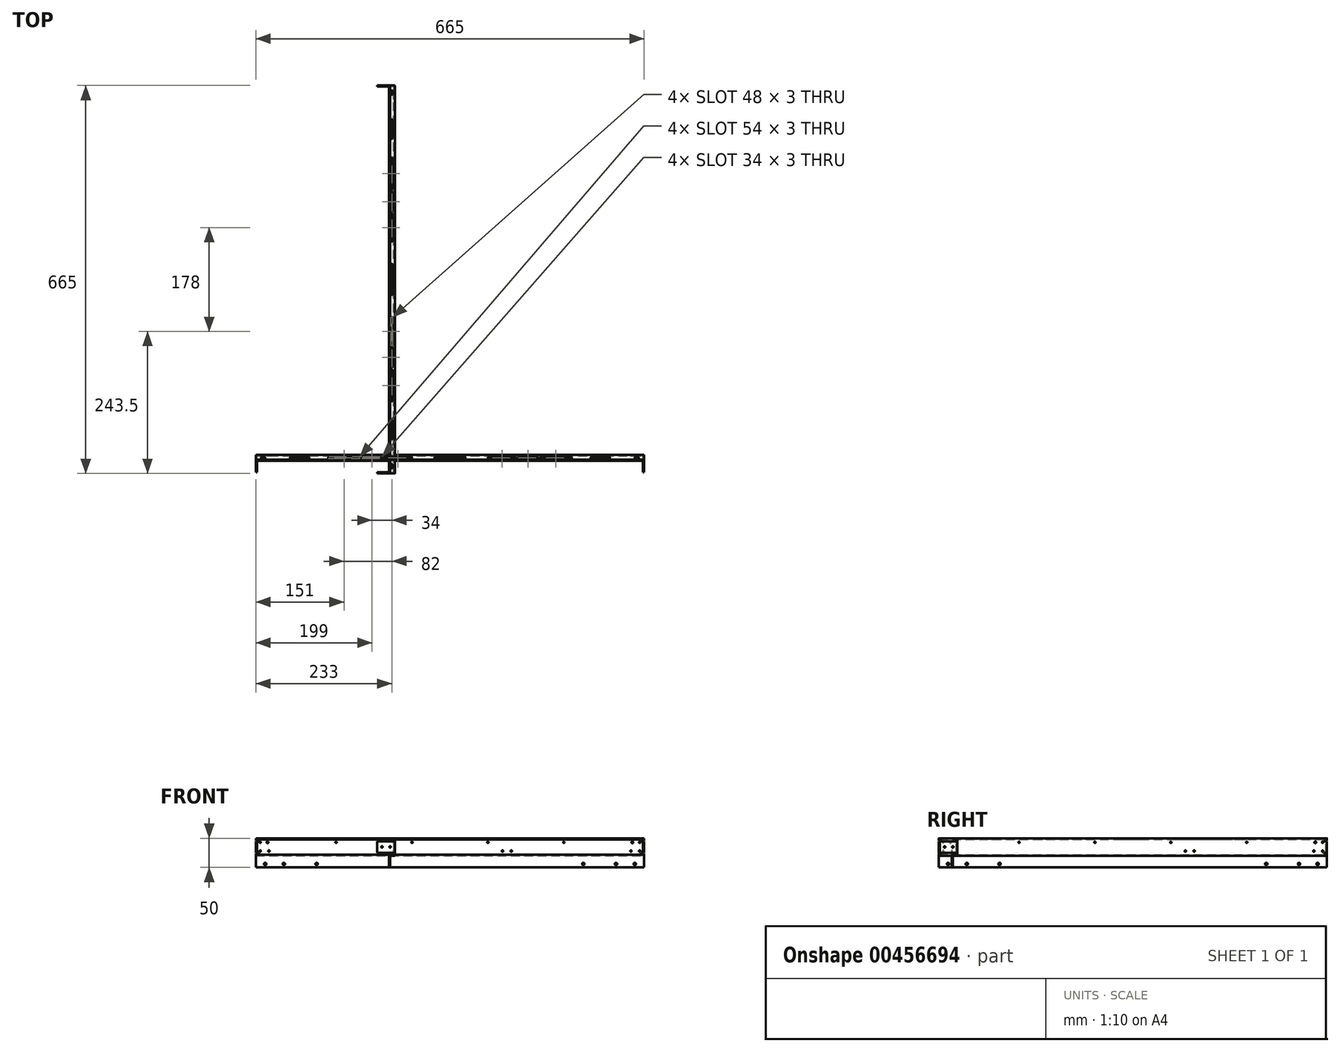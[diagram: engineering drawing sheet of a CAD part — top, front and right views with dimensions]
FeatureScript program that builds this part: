
annotation { "Feature Type Name" : "Feature", "Feature Type Description" : "" }
export const myFeature = defineFeature(function(context is Context, id is Id, definition is map)
    precondition{}
    {
        {
            var Q0;
            Q0=qCreatedBy(makeId("Front.planeOp"),FACE);
            var sketch = newSketch(context, id + "F0", { "sketchPlane" : qUnion([Q0])});
            skLineSegment(sketch, "E0", {"start": v(-20, 60) * mm, "end": v(-12, 60) * mm});
            skLineSegment(sketch, "E1", {"start": v(-12, 60) * mm, "end": v(-12, 58) * mm});
            skLineSegment(sketch, "E2", {"start": v(-12, 58) * mm, "end": v(-18, 58) * mm});
            skLineSegment(sketch, "E3", {"start": v(-18, 58) * mm, "end": v(-18, 32) * mm});
            skLineSegment(sketch, "E4", {"start": v(-20, 30) * mm, "end": v(-20, 60) * mm});
            skLineSegment(sketch, "E5.bottom", {"start": v(-18, 32) * mm, "end": v(-10, 32) * mm});
            skLineSegment(sketch, "E5.top", {"start": v(-20, 30) * mm, "end": v(-12, 30) * mm});
            skLineSegment(sketch, "E6.top", {"start": v(-10, 10) * mm, "end": v(-12, 10) * mm});
            skLineSegment(sketch, "E6.left", {"start": v(-10, 32) * mm, "end": v(-10, 10) * mm});
            skLineSegment(sketch, "E6.right", {"start": v(-12, 30) * mm, "end": v(-12, 10) * mm});
            skSolve(sketch);
        }
        {
            var Q0;
            Q0=qSketchRegion(id+"F0",true);
            extrude(context, id + "F1", {"entities" : qUnion([Q0]), "depth" : 665 * mm});
        }
        {
            var Q0;
            Q0=makeQuery(id+"F1.opExtrude","SWEPT_FACE",FACE,{"disambiguationData":[OSD([sQuery(id+"F0.wireOp",EDGE,"E3")])]});
            var sketch = newSketch(context, id + "F2", { "sketchPlane" : qUnion([Q0])});
            skLineSegment(sketch, "E7.bottom", {"start": v(0, 35) * mm, "end": v(-2, 35) * mm});
            skLineSegment(sketch, "E7.top", {"start": v(0, 55) * mm, "end": v(-2, 55) * mm});
            skLineSegment(sketch, "E7.left", {"start": v(0, 35) * mm, "end": v(0, 55) * mm});
            skLineSegment(sketch, "E7.right", {"start": v(-2, 35) * mm, "end": v(-2, 55) * mm});
            skLineSegment(sketch, "E8.bottom", {"start": v(-665, 55) * mm, "end": v(-663, 55) * mm});
            skLineSegment(sketch, "E8.top", {"start": v(-665, 35) * mm, "end": v(-663, 35) * mm});
            skLineSegment(sketch, "E8.left", {"start": v(-665, 55) * mm, "end": v(-665, 35) * mm});
            skLineSegment(sketch, "E8.right", {"start": v(-663, 55) * mm, "end": v(-663, 35) * mm});
            skSolve(sketch);
        }
        {
            var Q0;
            Q0=qSketchRegion(id+"F2",true);
            extrude(context, id + "F3", {"entities" : qUnion([Q0]), "operationType" : NewBodyOperationType.ADD, "depth" : 28 * mm});
        }
        {
            var Q0;
            Q0=makeQuery(id+"F1.opExtrude","SWEPT_FACE",FACE,{"disambiguationData":[OSD([sQuery(id+"F0.wireOp",EDGE,"E0")])]});
            var sketch = newSketch(context, id + "F4", { "sketchPlane" : qUnion([Q0])});
            skLineSegment(sketch, "E9.bottom", {"start": v(130, 0) * mm, "end": v(-20, 0) * mm, "construction": true});
            skLineSegment(sketch, "E9.top", {"start": v(130, -75) * mm, "end": v(-20, -75) * mm, "construction": true});
            skLineSegment(sketch, "E9.left", {"start": v(130, 0) * mm, "end": v(130, -75) * mm, "construction": true});
            skLineSegment(sketch, "E9.right", {"start": v(-20, 0) * mm, "end": v(-20, -75) * mm});
            skLineSegment(sketch, "E10.0", {"start": v(-20, -665) * mm, "end": v(-20, 0) * mm, "construction": true});
            skLineSegment(sketch, "E11.bottom", {"start": v(-20, -75) * mm, "end": v(130, -75) * mm, "construction": true});
            skLineSegment(sketch, "E11.top", {"start": v(-20, -140) * mm, "end": v(130, -140) * mm, "construction": true});
            skLineSegment(sketch, "E11.left", {"start": v(-20, -75) * mm, "end": v(-20, -140) * mm});
            skLineSegment(sketch, "E11.right", {"start": v(130, -75) * mm, "end": v(130, -140) * mm, "construction": true});
            skLineSegment(sketch, "E12.top", {"start": v(-20, -163) * mm, "end": v(130, -163) * mm, "construction": true});
            skLineSegment(sketch, "E12.left", {"start": v(-20, -140) * mm, "end": v(-20, -163) * mm});
            skLineSegment(sketch, "E12.right", {"start": v(130, -140) * mm, "end": v(130, -163) * mm, "construction": true});
            skLineSegment(sketch, "E13.top", {"start": v(-20, -243.5) * mm, "end": v(130, -243.5) * mm, "construction": true});
            skLineSegment(sketch, "E13.left", {"start": v(-20, -163) * mm, "end": v(-20, -243.5) * mm});
            skLineSegment(sketch, "E13.right", {"start": v(130, -163) * mm, "end": v(130, -243.5) * mm, "construction": true});
            skLineSegment(sketch, "E14.top", {"start": v(-20, -332.5) * mm, "end": v(130, -332.5) * mm, "construction": true});
            skLineSegment(sketch, "E14.left", {"start": v(-20, -243.5) * mm, "end": v(-20, -332.5) * mm});
            skLineSegment(sketch, "E14.right", {"start": v(130, -243.5) * mm, "end": v(130, -332.5) * mm, "construction": true});
            skLineSegment(sketch, "E15.top", {"start": v(-20, -462.5) * mm, "end": v(130, -462.5) * mm, "construction": true});
            skLineSegment(sketch, "E15.left", {"start": v(-20, -332.5) * mm, "end": v(-20, -462.5) * mm});
            skLineSegment(sketch, "E15.right", {"start": v(130, -332.5) * mm, "end": v(130, -462.5) * mm, "construction": true});
            skLineSegment(sketch, "E16.top", {"start": v(-20, -485.5) * mm, "end": v(130, -485.5) * mm, "construction": true});
            skLineSegment(sketch, "E16.left", {"start": v(-20, -462.5) * mm, "end": v(-20, -485.5) * mm});
            skLineSegment(sketch, "E16.right", {"start": v(130, -462.5) * mm, "end": v(130, -485.5) * mm, "construction": true});
            skLineSegment(sketch, "E17.top", {"start": v(-20, -665) * mm, "end": v(130, -665) * mm, "construction": true});
            skLineSegment(sketch, "E17.left", {"start": v(-20, -485.5) * mm, "end": v(-20, -665) * mm});
            skLineSegment(sketch, "E17.right", {"start": v(130, -485.5) * mm, "end": v(130, -665) * mm, "construction": true});
            skCircle(sketch, "E18", {"center": v(-15, -12.5) * mm, "radius": 1.5 * mm, "construction": true});
            skCircle(sketch, "E19", {"center": v(-15, -652.5) * mm, "radius": 1.5 * mm, "construction": true});
            skLineSegment(sketch, "E20.bottom", {"start": v(-13.5, -14.5) * mm, "end": v(-16.5, -14.5) * mm, "construction": true});
            skLineSegment(sketch, "E20.top", {"start": v(-13.5, -10.5) * mm, "end": v(-16.5, -10.5) * mm, "construction": true});
            skLineSegment(sketch, "E20.left", {"start": v(-13.5, -14.5) * mm, "end": v(-13.5, -10.5) * mm});
            skLineSegment(sketch, "E20.right", {"start": v(-16.5, -14.5) * mm, "end": v(-16.5, -10.5) * mm});
            skArc(sketch, "E21", {"start": v(-13.5, -10.5) * mm, "mid": v(-15, -9) * mm, "end": v(-16.5, -10.5) * mm});
            skArc(sketch, "E22", {"start": v(-16.5, -14.5) * mm, "mid": v(-15, -16) * mm, "end": v(-13.5, -14.5) * mm});
            skLineSegment(sketch, "E23.bottom", {"start": v(-13.5, -654.5) * mm, "end": v(-16.5, -654.5) * mm, "construction": true});
            skLineSegment(sketch, "E23.top", {"start": v(-13.5, -650.5) * mm, "end": v(-16.5, -650.5) * mm, "construction": true});
            skLineSegment(sketch, "E23.left", {"start": v(-13.5, -654.5) * mm, "end": v(-13.5, -650.5) * mm});
            skLineSegment(sketch, "E23.right", {"start": v(-16.5, -654.5) * mm, "end": v(-16.5, -650.5) * mm});
            skArc(sketch, "E24", {"start": v(-13.5, -650.5) * mm, "mid": v(-15, -649) * mm, "end": v(-16.5, -650.5) * mm});
            skArc(sketch, "E25", {"start": v(-16.5, -654.5) * mm, "mid": v(-15, -656) * mm, "end": v(-13.5, -654.5) * mm});
            skLineSegment(sketch, "E26", {"start": v(29.84, -27) * mm, "end": v(91.74, -27) * mm, "construction": true});
            skLineSegment(sketch, "E27", {"start": v(29.87, -48) * mm, "end": v(95.32, -48) * mm, "construction": true});
            skLineSegment(sketch, "E28.bottom", {"start": v(-13.5, -90) * mm, "end": v(-16.5, -90) * mm, "construction": true});
            skLineSegment(sketch, "E28.top", {"start": v(-13.5, -60) * mm, "end": v(-16.5, -60) * mm, "construction": true});
            skLineSegment(sketch, "E28.left", {"start": v(-13.5, -90) * mm, "end": v(-13.5, -60) * mm});
            skLineSegment(sketch, "E28.right", {"start": v(-16.5, -90) * mm, "end": v(-16.5, -60) * mm});
            skPoint(sketch, "E28.middle", {"position": v(-15, -75) * mm});
            skArc(sketch, "E29", {"start": v(-13.5, -60) * mm, "mid": v(-15, -58.5) * mm, "end": v(-16.5, -60) * mm});
            skArc(sketch, "E30", {"start": v(-16.5, -90) * mm, "mid": v(-15, -91.5) * mm, "end": v(-13.5, -90) * mm});
            skLineSegment(sketch, "E31.bottom", {"start": v(-13.5, -176.5) * mm, "end": v(-16.5, -176.5) * mm, "construction": true});
            skLineSegment(sketch, "E31.top", {"start": v(-13.5, -125.5) * mm, "end": v(-16.5, -125.5) * mm, "construction": true});
            skLineSegment(sketch, "E31.left", {"start": v(-13.5, -176.5) * mm, "end": v(-13.5, -125.5) * mm});
            skLineSegment(sketch, "E31.right", {"start": v(-16.5, -176.5) * mm, "end": v(-16.5, -125.5) * mm});
            skPoint(sketch, "E31.middle", {"position": v(-15, -151) * mm});
            skArc(sketch, "E32", {"start": v(-13.5, -125.5) * mm, "mid": v(-15, -124) * mm, "end": v(-16.5, -125.5) * mm});
            skArc(sketch, "E33", {"start": v(-16.5, -176.5) * mm, "mid": v(-15, -178) * mm, "end": v(-13.5, -176.5) * mm});
            skLineSegment(sketch, "E34", {"start": v(-372.96, -332.5) * mm, "end": v(602.04, -332.5) * mm, "construction": true});
            skLineSegment(sketch, "E35.bottom", {"start": v(-13.5, -266) * mm, "end": v(-16.5, -266) * mm, "construction": true});
            skLineSegment(sketch, "E35.top", {"start": v(-13.5, -221) * mm, "end": v(-16.5, -221) * mm, "construction": true});
            skLineSegment(sketch, "E35.left", {"start": v(-13.5, -266) * mm, "end": v(-13.5, -221) * mm});
            skLineSegment(sketch, "E35.right", {"start": v(-16.5, -266) * mm, "end": v(-16.5, -221) * mm});
            skPoint(sketch, "E35.middle", {"position": v(-15, -243.5) * mm});
            skArc(sketch, "E36", {"start": v(-13.5, -221) * mm, "mid": v(-15, -219.5) * mm, "end": v(-16.5, -221) * mm});
            skArc(sketch, "E37", {"start": v(-16.5, -266) * mm, "mid": v(-15, -267.5) * mm, "end": v(-13.5, -266) * mm});
            skLineSegment(sketch, "E38.bottom", {"start": v(-13.5, -357.5) * mm, "end": v(-16.5, -357.5) * mm, "construction": true});
            skLineSegment(sketch, "E38.top", {"start": v(-13.5, -307.5) * mm, "end": v(-16.5, -307.5) * mm, "construction": true});
            skLineSegment(sketch, "E38.left", {"start": v(-13.5, -357.5) * mm, "end": v(-13.5, -307.5) * mm});
            skLineSegment(sketch, "E38.right", {"start": v(-16.5, -357.5) * mm, "end": v(-16.5, -307.5) * mm});
            skPoint(sketch, "E38.middle", {"position": v(-15, -332.5) * mm});
            skArc(sketch, "E39", {"start": v(-13.5, -307.5) * mm, "mid": v(-15, -306) * mm, "end": v(-16.5, -307.5) * mm});
            skArc(sketch, "E40", {"start": v(-16.5, -357.5) * mm, "mid": v(-15, -359) * mm, "end": v(-13.5, -357.5) * mm});
            skLineSegment(sketch, "E41.bottom", {"start": v(-13.5, -214.5) * mm, "end": v(-16.5, -214.5) * mm, "construction": true});
            skLineSegment(sketch, "E41.top", {"start": v(-13.5, -183.5) * mm, "end": v(-16.5, -183.5) * mm, "construction": true});
            skLineSegment(sketch, "E41.left", {"start": v(-13.5, -214.5) * mm, "end": v(-13.5, -183.5) * mm});
            skLineSegment(sketch, "E41.right", {"start": v(-16.5, -214.5) * mm, "end": v(-16.5, -183.5) * mm});
            skPoint(sketch, "E41.middle", {"position": v(-15, -199) * mm});
            skArc(sketch, "E42", {"start": v(-13.5, -183.5) * mm, "mid": v(-15, -182) * mm, "end": v(-16.5, -183.5) * mm});
            skArc(sketch, "E43", {"start": v(-16.5, -214.5) * mm, "mid": v(-15, -216) * mm, "end": v(-13.5, -214.5) * mm});
            skArc(sketch, "E44.MirrorCS", {"start": v(-16.5, -450.5) * mm, "mid": v(-15, -449) * mm, "end": v(-13.5, -450.5) * mm});
            skLineSegment(sketch, "E45.MirrorCS", {"start": v(-13.5, -481.5) * mm, "end": v(-16.5, -481.5) * mm, "construction": true});
            skArc(sketch, "E46.MirrorCS", {"start": v(-13.5, -539.5) * mm, "mid": v(-15, -541) * mm, "end": v(-16.5, -539.5) * mm});
            skLineSegment(sketch, "E47.MirrorCS", {"start": v(-13.5, -444) * mm, "end": v(-16.5, -444) * mm, "construction": true});
            skArc(sketch, "E48.MirrorCS", {"start": v(-16.5, -399) * mm, "mid": v(-15, -397.5) * mm, "end": v(-13.5, -399) * mm});
            skArc(sketch, "E49.MirrorCS", {"start": v(-16.5, -488.5) * mm, "mid": v(-15, -487) * mm, "end": v(-13.5, -488.5) * mm});
            skArc(sketch, "E50.MirrorCS", {"start": v(-13.5, -444) * mm, "mid": v(-15, -445.5) * mm, "end": v(-16.5, -444) * mm});
            skArc(sketch, "E51.MirrorCS", {"start": v(-13.5, -481.5) * mm, "mid": v(-15, -483) * mm, "end": v(-16.5, -481.5) * mm});
            skLineSegment(sketch, "E52.MirrorCS", {"start": v(-13.5, -539.5) * mm, "end": v(-16.5, -539.5) * mm, "construction": true});
            skLineSegment(sketch, "E53.MirrorCS", {"start": v(-13.5, -488.5) * mm, "end": v(-16.5, -488.5) * mm, "construction": true});
            skLineSegment(sketch, "E54.MirrorCS", {"start": v(-13.5, -399) * mm, "end": v(-16.5, -399) * mm, "construction": true});
            skArc(sketch, "E55.MirrorCS", {"start": v(-16.5, -575) * mm, "mid": v(-15, -573.5) * mm, "end": v(-13.5, -575) * mm});
            skArc(sketch, "E56.MirrorCS", {"start": v(-13.5, -605) * mm, "mid": v(-15, -606.5) * mm, "end": v(-16.5, -605) * mm});
            skLineSegment(sketch, "E57.MirrorCS", {"start": v(-13.5, -605) * mm, "end": v(-16.5, -605) * mm, "construction": true});
            skLineSegment(sketch, "E58.MirrorCS", {"start": v(-13.5, -450.5) * mm, "end": v(-16.5, -450.5) * mm, "construction": true});
            skLineSegment(sketch, "E59.MirrorCS", {"start": v(-13.5, -575) * mm, "end": v(-16.5, -575) * mm, "construction": true});
            skLineSegment(sketch, "E60.MirrorCS", {"start": v(-16.5, -575) * mm, "end": v(-16.5, -605) * mm});
            skLineSegment(sketch, "E61.MirrorCS", {"start": v(-13.5, -575) * mm, "end": v(-13.5, -605) * mm});
            skLineSegment(sketch, "E62.MirrorCS", {"start": v(-13.5, -450.5) * mm, "end": v(-13.5, -481.5) * mm});
            skLineSegment(sketch, "E63.MirrorCS", {"start": v(-16.5, -450.5) * mm, "end": v(-16.5, -481.5) * mm});
            skPoint(sketch, "E64.MirrorP", {"position": v(-15, -466) * mm});
            skPoint(sketch, "E65.MirrorP", {"position": v(-15, -421.5) * mm});
            skPoint(sketch, "E66.MirrorP", {"position": v(-15, -590) * mm});
            skPoint(sketch, "E67.MirrorP", {"position": v(-15, -514) * mm});
            skLineSegment(sketch, "E68.MirrorCS", {"start": v(-16.5, -399) * mm, "end": v(-16.5, -444) * mm});
            skLineSegment(sketch, "E69.MirrorCS", {"start": v(-13.5, -399) * mm, "end": v(-13.5, -444) * mm});
            skLineSegment(sketch, "E70.MirrorCS", {"start": v(-16.5, -488.5) * mm, "end": v(-16.5, -539.5) * mm});
            skLineSegment(sketch, "E71.MirrorCS", {"start": v(-13.5, -488.5) * mm, "end": v(-13.5, -539.5) * mm});
            skPoint(sketch, "E72", {"position": v(-26.56, -12.5) * mm});
            skPoint(sketch, "E73", {"position": v(-24.04, -62.5) * mm});
            skPoint(sketch, "E74", {"position": v(-23.35, -87.5) * mm});
            skPoint(sketch, "E75", {"position": v(-24.4, -127.5) * mm});
            skPoint(sketch, "E76", {"position": v(-25, -145) * mm});
            skPoint(sketch, "E77", {"position": v(-24.92, -158) * mm});
            skPoint(sketch, "E78", {"position": v(-24.79, -174.5) * mm});
            skPoint(sketch, "E79", {"position": v(-24.35, -230) * mm});
            skPoint(sketch, "E80", {"position": v(-25.65, -255) * mm});
            skPoint(sketch, "E81", {"position": v(-24.26, -320) * mm});
            skPoint(sketch, "E82", {"position": v(-23.72, -352.5) * mm});
            skPoint(sketch, "E83", {"position": v(-24.95, -442.5) * mm});
            skPoint(sketch, "E84", {"position": v(-23.34, -467.5) * mm});
            skPoint(sketch, "E85", {"position": v(-22.9, -480.5) * mm});
            skPoint(sketch, "E86", {"position": v(-24.58, -489.5) * mm});
            skPoint(sketch, "E87", {"position": v(-25.98, -652.5) * mm});
            skSolve(sketch);
        }
        {
            var Q0;
            Q0=qSketchRegion(id+"F4",true);
            extrude(context, id + "F5", {"entities" : qUnion([Q0]), "operationType" : NewBodyOperationType.REMOVE, "oppositeDirection" : true, "depth" : 2 * mm});
        }
        {
            var Q0;
            Q0=makeQuery(id+"F1.opExtrude","SWEPT_FACE",FACE,{"disambiguationData":[OSD([sQuery(id+"F0.wireOp",EDGE,"E6.left")])]});
            var sketch = newSketch(context, id + "F6", { "sketchPlane" : qUnion([Q0])});
            skCircle(sketch, "E88", {"center": v(-16, 16) * mm, "radius": 2.05 * mm});
            skCircle(sketch, "E89", {"center": v(-617, 16) * mm, "radius": 2.05 * mm});
            skCircle(sketch, "E90", {"center": v(-104, 16) * mm, "radius": 2.05 * mm});
            skCircle(sketch, "E91", {"center": v(-7.5, 53) * mm, "radius": 1.2 * mm});
            skCircle(sketch, "E92.1.0.0", {"center": v(-137.5, 53) * mm, "radius": 1.2 * mm});
            skCircle(sketch, "E92.2.0.0", {"center": v(-267.5, 53) * mm, "radius": 1.2 * mm});
            skLineSegment(sketch, "E92.direction1", {"start": v(-7.5, 53) * mm, "end": v(-137.5, 53) * mm, "construction": true});
            skCircle(sketch, "E93.0.3.0", {"center": v(-397.5, 53) * mm, "radius": 1.2 * mm});
            skCircle(sketch, "E93.0.4.0", {"center": v(-527.5, 53) * mm, "radius": 1.2 * mm});
            skCircle(sketch, "E93.0.5.0", {"center": v(-657.5, 53) * mm, "radius": 1.2 * mm});
            skCircle(sketch, "E94", {"center": v(-48, 16) * mm, "radius": 2.05 * mm});
            skCircle(sketch, "E95", {"center": v(-649, 16) * mm, "radius": 2.05 * mm});
            skCircle(sketch, "E96", {"center": v(-561, 16) * mm, "radius": 2.05 * mm});
            skLineSegment(sketch, "E97", {"start": v(-2, 23.79) * mm, "end": v(-2, 13.85) * mm, "construction": true});
            skLineSegment(sketch, "E98", {"start": v(-663, 24.44) * mm, "end": v(-663, 15.87) * mm, "construction": true});
            skLineSegment(sketch, "E99.0", {"start": v(-665, 58) * mm, "end": v(-665, 55) * mm});
            skLineSegment(sketch, "E100.0", {"start": v(-665, 55) * mm, "end": v(-663, 55) * mm});
            skPoint(sketch, "E101.oppositeSnap0", {"position": v(-664, 55) * mm});
            skLineSegment(sketch, "E101.bottom", {"start": v(-665, 56) * mm, "end": v(-660, 56) * mm});
            skLineSegment(sketch, "E101.top", {"start": v(-665, 55) * mm, "end": v(-660, 55) * mm});
            skLineSegment(sketch, "E101.left", {"start": v(-665, 56) * mm, "end": v(-665, 55) * mm});
            skLineSegment(sketch, "E101.right", {"start": v(-660, 56) * mm, "end": v(-660, 55) * mm});
            skLineSegment(sketch, "E102.0", {"start": v(-665, 35) * mm, "end": v(-663, 35) * mm});
            skLineSegment(sketch, "E102.1", {"start": v(-665, 35) * mm, "end": v(-665, 32) * mm});
            skLineSegment(sketch, "E103.bottom", {"start": v(-665, 35) * mm, "end": v(-660, 35) * mm});
            skLineSegment(sketch, "E103.top", {"start": v(-665, 34) * mm, "end": v(-660, 34) * mm});
            skLineSegment(sketch, "E103.left", {"start": v(-665, 35) * mm, "end": v(-665, 34) * mm});
            skLineSegment(sketch, "E103.right", {"start": v(-660, 35) * mm, "end": v(-660, 34) * mm});
            skLineSegment(sketch, "E104.0", {"start": v(0, 58) * mm, "end": v(0, 55) * mm});
            skLineSegment(sketch, "E104.1", {"start": v(0, 55) * mm, "end": v(-2, 55) * mm});
            skLineSegment(sketch, "E104.2", {"start": v(0, 35) * mm, "end": v(-2, 35) * mm});
            skLineSegment(sketch, "E104.3", {"start": v(0, 35) * mm, "end": v(0, 32) * mm});
            skLineSegment(sketch, "E105.bottom", {"start": v(0, 55) * mm, "end": v(-5, 55) * mm});
            skLineSegment(sketch, "E105.top", {"start": v(0, 56) * mm, "end": v(-5, 56) * mm});
            skLineSegment(sketch, "E105.left", {"start": v(0, 55) * mm, "end": v(0, 56) * mm});
            skLineSegment(sketch, "E105.right", {"start": v(-5, 55) * mm, "end": v(-5, 56) * mm});
            skLineSegment(sketch, "E106.bottom", {"start": v(0, 35) * mm, "end": v(-5, 35) * mm});
            skLineSegment(sketch, "E106.top", {"start": v(0, 34) * mm, "end": v(-5, 34) * mm});
            skLineSegment(sketch, "E106.left", {"start": v(0, 35) * mm, "end": v(0, 34) * mm});
            skLineSegment(sketch, "E106.right", {"start": v(-5, 35) * mm, "end": v(-5, 34) * mm});
            skCircle(sketch, "E107", {"center": v(-7.5, 38) * mm, "radius": 1.2 * mm});
            skCircle(sketch, "E108", {"center": v(-657.5, 38) * mm, "radius": 1.2 * mm});
            skCircle(sketch, "E109", {"center": v(-22.5, 38) * mm, "radius": 1.2 * mm});
            skCircle(sketch, "E110", {"center": v(-642.5, 38) * mm, "radius": 1.2 * mm});
            skCircle(sketch, "E111", {"center": v(-227.5, 38) * mm, "radius": 1.2 * mm});
            skCircle(sketch, "E112", {"center": v(-242.5, 38) * mm, "radius": 1.2 * mm});
            skCircle(sketch, "E113", {"center": v(-20, 53) * mm, "radius": 1.5 * mm});
            skCircle(sketch, "E114", {"center": v(-645, 53) * mm, "radius": 1.5 * mm});
            skSolve(sketch);
        }
        {
            var Q0;
            Q0=qSketchRegion(id+"F6",true);
            extrude(context, id + "F7", {"entities" : qUnion([Q0]), "operationType" : NewBodyOperationType.REMOVE, "oppositeDirection" : true, "depth" : 25 * mm});
        }
        {
            var Q0;
            Q0=makeQuery(id+"F3.boolean.opBoolean","MERGE",FACE,{"derivedFrom":[makeQuery(id+"F1.opExtrude","CAP_FACE",FACE,{"disambiguationData":[OSD([sQuery(id+"F0.wireOp",EDGE,"E0"),sQuery(id+"F0.wireOp",EDGE,"E1"),sQuery(id+"F0.wireOp",EDGE,"E2"),sQuery(id+"F0.wireOp",EDGE,"E3"),sQuery(id+"F0.wireOp",EDGE,"E4"),sQuery(id+"F0.wireOp",EDGE,"E5.bottom"),sQuery(id+"F0.wireOp",EDGE,"E5.top"),sQuery(id+"F0.wireOp",EDGE,"E6.top"),sQuery(id+"F0.wireOp",EDGE,"E6.left"),sQuery(id+"F0.wireOp",EDGE,"E6.right")])],"isStart":false}),makeQuery(id+"F3.opExtrude","SWEPT_FACE",FACE,{"disambiguationData":[OSD([sQuery(id+"F2.wireOp",EDGE,"E8.left")])]})]});
            var sketch = newSketch(context, id + "F8", { "sketchPlane" : qUnion([Q0])});
            skCircle(sketch, "E115", {"center": v(-12, 45) * mm, "radius": 1.2 * mm});
            skPoint(sketch, "E116", {"position": v(10, 45) * mm});
            skCircle(sketch, "E117", {"center": v(2, 45) * mm, "radius": 1.2 * mm});
            skSolve(sketch);
        }
        {
            var Q0;
            Q0=qSketchRegion(id+"F8",true);
            extrude(context, id + "F9", {"entities" : qUnion([Q0]), "operationType" : NewBodyOperationType.REMOVE, "endBound" : BoundingType.THROUGH_ALL, "oppositeDirection" : true, "depth" : 2 * mm});
        }
        {
            var Q0;
            Q0=makeQuery(id+"F1.opExtrude","SWEPT_EDGE",EDGE,{"disambiguationData":[OSD([sQuery(id+"F0.wireOp",EDGE,"E0"),sQuery(id+"F0.wireOp",EDGE,"E4")])]});
            var Q1;
            Q1=makeQuery(id+"F1.opExtrude","SWEPT_EDGE",EDGE,{"disambiguationData":[OSD([sQuery(id+"F0.wireOp",EDGE,"E2"),sQuery(id+"F0.wireOp",EDGE,"E3")])]});
            var Q2;
            Q2=makeQuery(id+"F1.opExtrude","SWEPT_EDGE",EDGE,{"disambiguationData":[OSD([sQuery(id+"F0.wireOp",EDGE,"E3"),sQuery(id+"F0.wireOp",EDGE,"E5.bottom")])]});
            var Q3;
            Q3=makeQuery(id+"F1.opExtrude","SWEPT_EDGE",EDGE,{"disambiguationData":[OSD([sQuery(id+"F0.wireOp",EDGE,"E5.bottom"),sQuery(id+"F0.wireOp",EDGE,"E6.left")])]});
            var Q4;
            Q4=makeQuery(id+"F1.opExtrude","SWEPT_EDGE",EDGE,{"disambiguationData":[OSD([sQuery(id+"F0.wireOp",EDGE,"E4"),sQuery(id+"F0.wireOp",EDGE,"E5.top")])]});
            var Q5;
            Q5=makeQuery(id+"F1.opExtrude","SWEPT_EDGE",EDGE,{"disambiguationData":[OSD([sQuery(id+"F0.wireOp",EDGE,"E5.top"),sQuery(id+"F0.wireOp",EDGE,"E6.right")])]});
            fillet(context, id + "F10", {"entities" : qUnion([Q0, Q1, Q2, Q3, Q4, Q5]), "radius" : 1 * mm, "tangentPropagation" : true, "allowEdgeOverflow" : false});
        }
        {
            var Q0;
            Q0=makeQuery(id+"F3.opExtrude","CAP_EDGE",EDGE,{"disambiguationData":[OSD([sQuery(id+"F2.wireOp",EDGE,"E8.right")])],"isStart":true});
            var Q1;
            {var subQ0=sQuery(id+"F0.wireOp",EDGE,"E4");Q1=makeQuery(id+"F7.boolean.opBoolean","SPLIT",EDGE,{"disambiguationData":[TD([makeQuery(id+"F3.opExtrude","SWEPT_FACE",FACE,{"disambiguationData":[OSD([sQuery(id+"F2.wireOp",EDGE,"E8.bottom")])]})])],"derivedFrom":makeQuery(id+"F1.opExtrude","CAP_EDGE",EDGE,{"disambiguationData":[OSD([subQ0])],"isStart":false})});}
            var Q2;
            Q2=makeQuery(id+"F3.opExtrude","CAP_EDGE",EDGE,{"disambiguationData":[OSD([sQuery(id+"F2.wireOp",EDGE,"E7.right")])],"isStart":true});
            var Q3;
            {var subQ0=sQuery(id+"F0.wireOp",EDGE,"E4");Q3=makeQuery(id+"F7.boolean.opBoolean","SPLIT",EDGE,{"disambiguationData":[TD([makeQuery(id+"F3.opExtrude","SWEPT_FACE",FACE,{"disambiguationData":[OSD([sQuery(id+"F2.wireOp",EDGE,"E7.bottom")])]})])],"derivedFrom":makeQuery(id+"F1.opExtrude","CAP_EDGE",EDGE,{"disambiguationData":[OSD([subQ0])],"isStart":true})});}
            fillet(context, id + "F11", {"entities" : qUnion([Q0, Q1, Q2, Q3]), "radius" : 1 * mm, "tangentPropagation" : true, "allowEdgeOverflow" : false});
        }
        {
            var Q0;
            Q0=qCreatedBy(makeId("Right.planeOp"),FACE);
            cPlane(context, id + "F12", {"entities" : qUnion([Q0]), "cplaneType" : CPlaneType.OFFSET, "offset" : 113 * mm, "width" : 150 * mm, "height" : 150 * mm});
        }
        {
            var Q0;
            Q0=makeQuery(id+"F1.opExtrude","SWEPT_BODY",BODY,{"disambiguationData":[OSD([sQuery(id+"F0.wireOp",EDGE,"E0"),sQuery(id+"F0.wireOp",EDGE,"E1"),sQuery(id+"F0.wireOp",EDGE,"E2"),sQuery(id+"F0.wireOp",EDGE,"E3"),sQuery(id+"F0.wireOp",EDGE,"xb1tLthF-IiVW-rdyS-DzM4-F0JxlruL6ZiX"),sQuery(id+"F0.wireOp",EDGE,"E4")])]});
            var Q1;
            Q1=qCreatedBy(id+"F12.planeOp",FACE);
            mirror(context, id + "F13", {"entities" : qUnion([Q0]), "mirrorPlane" : qUnion([Q1])});
        }
        {
            var Q0;
            Q0=makeQuery(id+"F1.opExtrude","SWEPT_BODY",BODY,{"disambiguationData":[OSD([sQuery(id+"F0.wireOp",EDGE,"E0"),sQuery(id+"F0.wireOp",EDGE,"E1"),sQuery(id+"F0.wireOp",EDGE,"E2"),sQuery(id+"F0.wireOp",EDGE,"E3"),sQuery(id+"F0.wireOp",EDGE,"E4"),sQuery(id+"F0.wireOp",EDGE,"E5.bottom"),sQuery(id+"F0.wireOp",EDGE,"E5.top"),sQuery(id+"F0.wireOp",EDGE,"E6.top"),sQuery(id+"F0.wireOp",EDGE,"E6.left"),sQuery(id+"F0.wireOp",EDGE,"E6.right")])]});
            var Q1;
            Q1=makeQuery(id+"F3.opExtrude","CAP_EDGE",EDGE,{"disambiguationData":[OSD([sQuery(id+"F2.wireOp",EDGE,"E8.right")])],"isStart":false});
            transform(context, id + "F14", {"entities" : qUnion([Q0]), "transformType" : TransformType.ROTATION, "transformAxis" : qUnion([Q1]), "angle" : 90 * degree, "makeCopy" : false});
        }
    });
